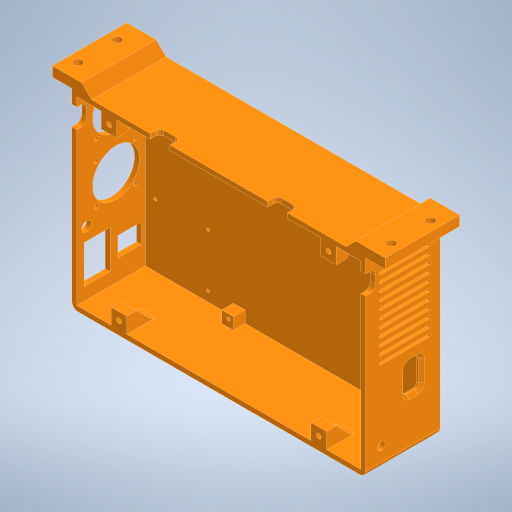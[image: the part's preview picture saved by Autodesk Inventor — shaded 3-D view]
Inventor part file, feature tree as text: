
AUTODESK INVENTOR PART (.ipt)
format: ipt  version: 2024.1 (Build 281209000, 209)  size: 697,856 bytes
history: native  units: in
note: dims shown in document units (in); Inventor stores cm internally (conversion verified against a paired STEP export)
features: extrude x21, sketch x21, fillet x6, chamfer x4
ambient origin geometry x8: Origin, YZ Plane, XZ Plane, XY Plane, X Axis, Y Axis, Z Axis, Center Point
bodies: Solid1 (feature_tree)
feature tree (52):
  extrude  "Extrusion1"  Depth=5.9055in
  extrude  "Extrusion2"  Depth=0.0984in
  extrude  "Extrusion3"  Depth=0.0984in
  extrude  "Extrusion4"  Depth=1.378in TaperAngle=0.0deg
  extrude  "Extrusion5"  Depth=0.2362in
  extrude  "Extrusion6"  Depth=0.2362in
  extrude  "Extrusion7"  Depth=0.2362in
  fillet  "Fillet1"  Radius=0.2362in
  chamfer  "Chamfer1"  Distance=0.2362in
  extrude  "Extrusion8"  Depth=0.1575in
  fillet  "Fillet2"  Radius=0.1575in
  extrude  "Extrusion9"  Depth=0.0709in
  extrude  "Extrusion10"  Depth=0.0787in
  chamfer  "Chamfer2"  [1 undecoded]
  extrude  "Extrusion11"  Depth=0.0709in
  extrude  "Extrusion12"  Depth=0.0787in
  fillet  "Fillet3"  Radius=0.0984in
  fillet  "Fillet4"  Radius=0.0886in
  extrude  "Extrusion13"  Depth=0.315in
  extrude  "Extrusion14"  Depth=0.8858in
  extrude  "Extrusion15"  TaperAngle=0.0deg  [1 undecoded]
  extrude  "Extrusion16"  Depth=0.0591in TaperAngle=45.0deg
  extrude  "Extrusion17"  Depth=0.2756in
  chamfer  "Chamfer3"  Distance=1.811in
  extrude  "Extrusion18"  Depth=4.3307in
  extrude  "Extrusion19"  TaperAngle=0.0deg  [1 undecoded]
  chamfer  "Chamfer4"  Distance=0.0295in
  extrude  "Extrusion20"  Depth=0.9449in
  fillet  "Fillet5"  Radius=0.6299in
  extrude  "Extrusion21"  Depth=0.7874in
  fillet  "Fillet6"  [1 undecoded]
  sketch  "Sketch1"  dims[d0=3.8287in d1=5.9055in]
  sketch  "Sketch2"  dims[d2=1.4961in d3=0.0in d4=0.0984in]
  sketch  "Sketch3"  dims[d5=0.0984in d6=0.0984in]
  sketch  "Sketch4"  dims[d7=0.0984in d8=1.378in d9=0.0in]
  sketch  "Sketch5"  dims[d10=0.2362in d11=0.2362in]
  sketch  "Sketch6"  dims[d12=0.2362in d13=0.2362in]
  sketch  "Sketch7"  dims[d14=0.2362in d15=0.2362in d16=0.2362in]
  sketch  "Sketch8"  dims[d17=0.2362in]
  sketch  "Sketch10"  dims[d18=3.4646in]
  sketch  "Sketch11"  dims[d19=3.4646in d20=0.2362in d21=0.0in]
  sketch  "Sketch12"  dims[d22=0.0709in d23=0.1476in d24=0.1575in]
  sketch  "Sketch13"  dims[d25=0.0in d26=0.0in d27=0.0709in]
  sketch  "Sketch14"  dims[d28=0.0787in d29=0.0787in d30=0.0in d31=0.0in]
  sketch  "Sketch15"  dims[d32=0.0709in d33=0.0709in]
  sketch  "Sketch16"  dims[d34=0.0984in d35=0.0787in d36=0.0984in d37=0.0886in]
  sketch  "Sketch17"  dims[d38=0.0in d39=0.0in d40=0.315in]
  sketch  "Sketch18"  dims[d41=0.5906in d42=0.8858in]
  sketch  "Sketch19"  dims[d43=0.2559in d44=0.0in d45=0.0in]
  sketch  "Sketch20"  dims[d46=0.0787in d47=0.0591in d48=0.0787in d49=45.0deg]
  sketch  "Sketch21"  dims[d50=0.0591in d51=0.2756in]
  sketch  "Sketch22"  dims[d52=0.1969in d53=1.811in d54=4.3307in d56=0.1575in d57=0.3937in d59=0.3937in d61=0.0in d62=0.0in d63=0.0295in d64=0.9449in d66=0.6299in d67=0.7874in d70=0.0in d71=0.0in d72=0.0866in d73=0.0866in d75=0.0866in d76=0.3937in d77=0.3937in d79=0.3937in d80=0.3937in d81=0.3937in d82=0.3937in d83=0.0866in d84=0.3937in d85=0.3937in d86=0.3937in d87=0.0in d88=0.0591in d89=0.0787in d90=45.0deg d91=0.7874in d93=1.1811in d94=0.3937in d96=0.3937in d98=0.7874in d100=1.1811in d101=0.3937in d103=0.3937in d105=0.5197in d106=0.7677in d107=0.8268in d108=0.3543in d109=0.3937in d110=0.0in d111=0.1969in d112=0.3937in d113=0.2756in d114=0.0in d115=0.0in d116=0.1181in d117=0.1181in d118=0.4724in d119=0.3937in d120=0.1969in d121=0.5118in d122=0.3937in d123=0.0in d124=0.1575in d125=0.315in d126=0.3937in d127=0.3937in d128=0.0in d129=0.1969in d130=0.1969in d131=1.378in d132=0.3937in d133=0.0in d134=0.063in d135=0.063in d136=0.063in d137=0.1969in d138=1.2598in d139=1.2598in d140=1.2598in d141=0.1969in d142=1.2598in d143=0.3937in d144=0.0in d145=0.5906in d146=0.5906in d147=1.4961in d148=1.4961in d149=0.1969in d150=0.1969in d151=0.1969in d152=0.0in d153=0.1969in d154=0.0787in d155=45.0deg d156=0.1654in d157=0.1654in d158=0.1654in d159=0.1654in d160=0.315in d161=0.1969in d162=0.3937in d163=0.1969in d164=0.1969in d165=0.315in d166=0.1969in d167=0.3937in d168=0.1969in d169=0.0in d170=0.315in d171=0.4134in d172=0.315in d173=0.4134in d174=0.4134in d175=0.315in d176=0.315in d177=0.4134in d178=0.5906in d179=0.5906in d180=0.7874in d181=0.7874in d182=0.1969in d183=0.0in d184=0.315in d185=0.0787in d186=45.0deg d187=0.1024in d188=0.1024in d189=0.1024in d190=0.1024in d191=0.1575in d192=0.1575in d193=0.1575in d194=0.1575in d195=0.1575in d196=0.1575in d197=0.1575in d198=0.1575in d199=0.1969in d200=0.0in d201=0.1969in d202=0.3937in d203=0.3937in d204=1.5748in d205=1.5748in d206=0.1969in d207=0.0in d208=0.0787in]
note: 4 required parameter values undecoded (feature->parameter linkage not recoverable at this tier; creation-order binding heuristic only, values carry confidence <= 0.55)
